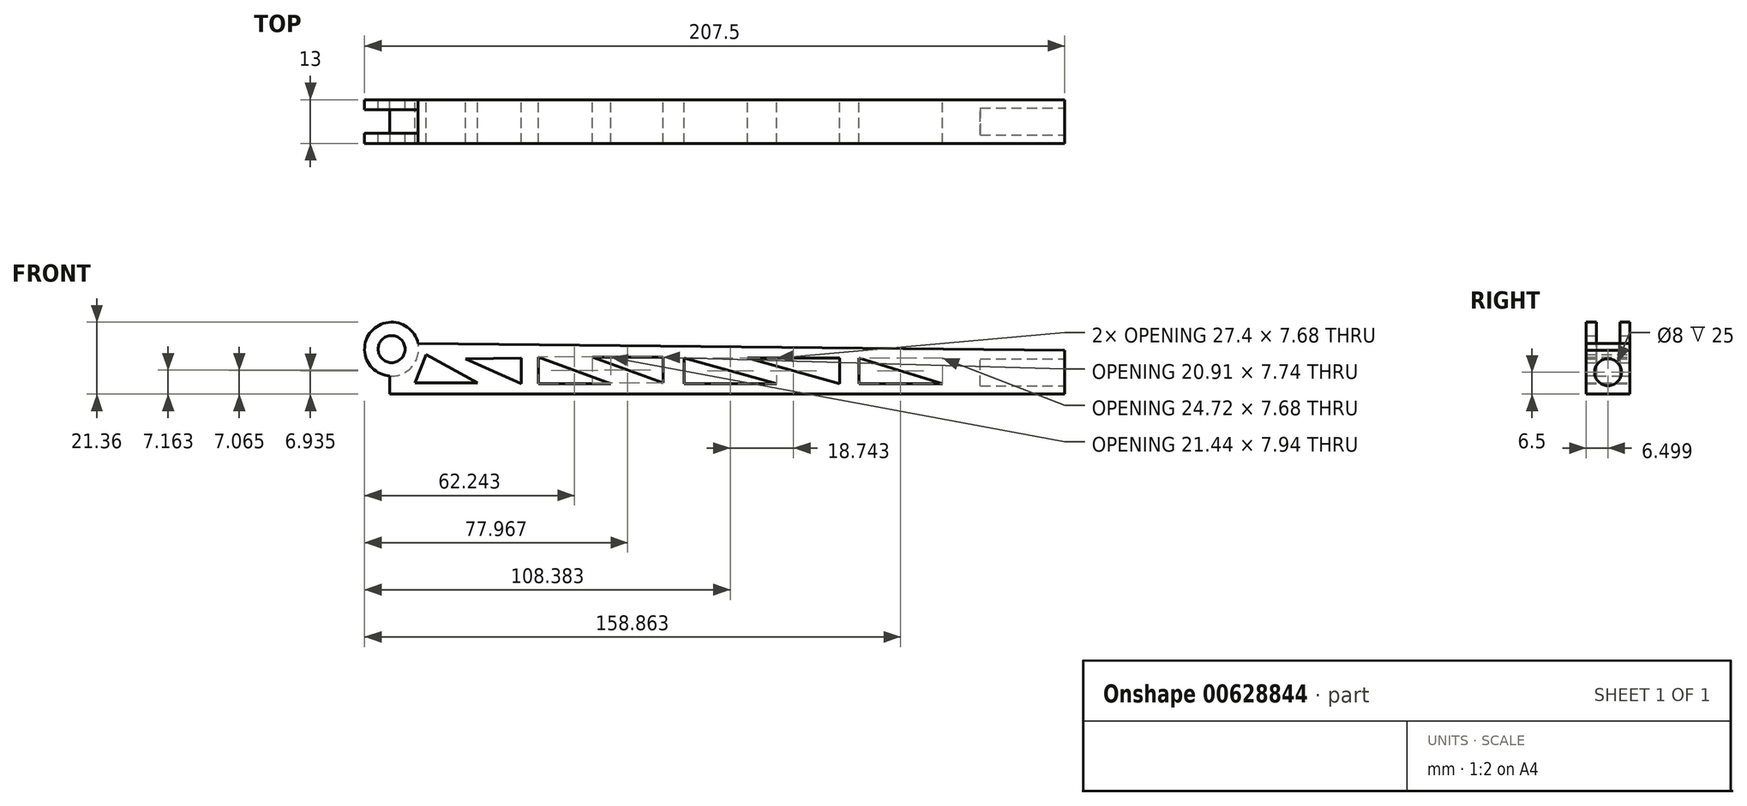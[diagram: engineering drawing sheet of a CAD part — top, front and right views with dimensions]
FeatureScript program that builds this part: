
annotation { "Feature Type Name" : "Feature", "Feature Type Description" : "" }
export const myFeature = defineFeature(function(context is Context, id is Id, definition is map)
    precondition{}
    {
        {
            var Q0;
            Q0=qCreatedBy(makeId("Top.planeOp"),FACE);
            var sketch = newSketch(context, id + "F0", { "sketchPlane" : qUnion([Q0])});
            skLineSegment(sketch, "E0.bottom", {"start": v(-30.92, 10.53) * mm, "end": v(169.08, 10.53) * mm});
            skLineSegment(sketch, "E0.top", {"start": v(-30.92, 23.53) * mm, "end": v(169.08, 23.53) * mm});
            skLineSegment(sketch, "E0.left", {"start": v(-30.92, 10.53) * mm, "end": v(-30.92, 23.53) * mm});
            skLineSegment(sketch, "E0.right", {"start": v(169.08, 10.53) * mm, "end": v(169.08, 23.53) * mm});
            skSolve(sketch);
        }
        {
            var Q0;
            Q0=makeQuery(id+"F0.imprint","IMPRINT",FACE,{"disambiguationData":[TD([[makeQuery(id+"F0.imprint","IMPRINT",EDGE,{"derivedFrom":sQuery(id+"F0.wireOp",EDGE,"E0.bottom")}),1.0]])]});
            extrude(context, id + "F1", {"entities" : qUnion([Q0]), "depth" : 15 * mm, "offsetDistance" : 25 * mm});
        }
        {
            var Q0;
            Q0=makeQuery(id+"F1.opExtrude","SWEPT_FACE",FACE,{"disambiguationData":[OSD([sQuery(id+"F0.wireOp",EDGE,"E0.bottom")])]});
            var sketch = newSketch(context, id + "F2", { "sketchPlane" : qUnion([Q0])});
            skCircle(sketch, "E1", {"center": v(-30.42, 13.36) * mm, "radius": 8 * mm});
            skSolve(sketch);
        }
        {
            var Q0;
            Q0 = qSketchRegion(id + "F2", true);
            extrude(context, id + "F3", {"entities" : qUnion([Q0]), "operationType" : NewBodyOperationType.ADD, "oppositeDirection" : true, "depth" : 3 * mm, "offsetDistance" : 25 * mm});
        }
        {
            var Q0;
            Q0=makeQuery(id+"F1.opExtrude","SWEPT_FACE",FACE,{"disambiguationData":[OSD([sQuery(id+"F0.wireOp",EDGE,"E0.top")])]});
            var sketch = newSketch(context, id + "F4", { "sketchPlane" : qUnion([Q0])});
            skCircle(sketch, "E2", {"center": v(30.42, 13.36) * mm, "radius": 8 * mm});
            skSolve(sketch);
        }
        {
            var Q0;
            Q0 = qSketchRegion(id + "F4", true);
            extrude(context, id + "F5", {"entities" : qUnion([Q0]), "operationType" : NewBodyOperationType.ADD, "oppositeDirection" : true, "depth" : 3 * mm, "offsetDistance" : 25 * mm});
        }
        {
            var Q0;
            Q0=makeQuery(id+"F5.boolean.opBoolean","MERGE",FACE,{"derivedFrom":[makeQuery(id+"F1.opExtrude","SWEPT_FACE",FACE,{"disambiguationData":[OSD([sQuery(id+"F0.wireOp",EDGE,"E0.top")])]}),makeQuery(id+"F5.opExtrude","CAP_FACE",FACE,{"disambiguationData":[OSD([sQuery(id+"F4.wireOp",EDGE,"E2")])],"isStart":true})]});
            var sketch = newSketch(context, id + "F6", { "sketchPlane" : qUnion([Q0])});
            skCircle(sketch, "E3", {"center": v(30.42, 13.36) * mm, "radius": 4 * mm});
            skSolve(sketch);
        }
        {
            var Q0;
            Q0 = qSketchRegion(id + "F6", true);
            extrude(context, id + "F7", {"entities" : qUnion([Q0]), "operationType" : NewBodyOperationType.REMOVE, "oppositeDirection" : true, "depth" : 13 * mm, "offsetDistance" : 25 * mm});
        }
        {
            var Q0;
            Q0=makeQuery(id+"F5.opExtrude","CAP_FACE",FACE,{"disambiguationData":[OSD([sQuery(id+"F4.wireOp",EDGE,"E2")])],"isStart":false});
            var sketch = newSketch(context, id + "F8", { "sketchPlane" : qUnion([Q0])});
            skCircle(sketch, "E4", {"center": v(-30.42, 13.36) * mm, "radius": 8 * mm});
            skSolve(sketch);
        }
        {
            var Q0;
            Q0 = qSketchRegion(id + "F8", true);
            extrude(context, id + "F9", {"entities" : qUnion([Q0]), "operationType" : NewBodyOperationType.REMOVE, "depth" : 7 * mm, "offsetDistance" : 25 * mm});
        }
        {
            var Q0;
            Q0=makeQuery(id+"F3.boolean.opBoolean","MERGE",FACE,{"derivedFrom":[makeQuery(id+"F1.opExtrude","SWEPT_FACE",FACE,{"disambiguationData":[OSD([sQuery(id+"F0.wireOp",EDGE,"E0.bottom")])]}),makeQuery(id+"F3.opExtrude","CAP_FACE",FACE,{"disambiguationData":[OSD([sQuery(id+"F2.wireOp",EDGE,"E1")])],"isStart":true})]});
            var sketch = newSketch(context, id + "F10", { "sketchPlane" : qUnion([Q0])});
            skLineSegment(sketch, "E5", {"start": v(-22.59, 15) * mm, "end": v(169.08, 13) * mm});
            skSolve(sketch);
        }
        {
            var Q0;
            {var subQ0=sQuery(id+"F10.wireOp",EDGE,"E5");Q0=makeQuery(id+"F10.imprint","IMPRINT",FACE,{"disambiguationData":[TD([[makeQuery(id+"F10.imprint","IMPRINT",EDGE,{"derivedFrom":subQ0}),1.0]])]});}
            extrude(context, id + "F11", {"entities" : qUnion([Q0]), "operationType" : NewBodyOperationType.REMOVE, "oppositeDirection" : true, "depth" : 25 * mm, "offsetDistance" : 25 * mm});
        }
        {
            var Q0;
            Q0=makeQuery(id+"F1.opExtrude","SWEPT_FACE",FACE,{"disambiguationData":[OSD([sQuery(id+"F0.wireOp",EDGE,"E0.right")])]});
            var sketch = newSketch(context, id + "F12", { "sketchPlane" : qUnion([Q0])});
            skCircle(sketch, "E6", {"center": v(17.03, 6.5) * mm, "radius": 4 * mm});
            skSolve(sketch);
        }
        {
            var Q0;
            Q0=makeQuery(id+"F12.imprint","IMPRINT",FACE,{"disambiguationData":[TD([[makeQuery(id+"F12.imprint","IMPRINT",EDGE,{"derivedFrom":sQuery(id+"F12.wireOp",EDGE,"E6")}),1.0]])]});
            extrude(context, id + "F13", {"entities" : qUnion([Q0]), "operationType" : NewBodyOperationType.REMOVE, "oppositeDirection" : true, "depth" : 25 * mm, "offsetDistance" : 25 * mm});
        }
        {
            var Q0;
            Q0=makeQuery(id+"F5.boolean.opBoolean","MERGE",FACE,{"derivedFrom":[makeQuery(id+"F1.opExtrude","SWEPT_FACE",FACE,{"disambiguationData":[OSD([sQuery(id+"F0.wireOp",EDGE,"E0.top")])]}),makeQuery(id+"F5.opExtrude","CAP_FACE",FACE,{"disambiguationData":[OSD([sQuery(id+"F4.wireOp",EDGE,"E2")])],"isStart":true})]});
            var sketch = newSketch(context, id + "F14", { "sketchPlane" : qUnion([Q0])});
            skLineSegment(sketch, "E7", {"start": v(20.2, 11.75) * mm, "end": v(23.44, 3.36) * mm});
            skLineSegment(sketch, "E8", {"start": v(23.44, 3.36) * mm, "end": v(5, 3.36) * mm});
            skLineSegment(sketch, "E9", {"start": v(5, 3.36) * mm, "end": v(20.2, 11.75) * mm});
            skLineSegment(sketch, "E10", {"start": v(8.48, 10.46) * mm, "end": v(-8.02, 3.1) * mm});
            skLineSegment(sketch, "E11", {"start": v(-8.02, 3.1) * mm, "end": v(-8.02, 10.75) * mm});
            skLineSegment(sketch, "E12", {"start": v(-8.02, 10.75) * mm, "end": v(8.48, 10.46) * mm});
            skLineSegment(sketch, "E13", {"start": v(-13.1, 3.1) * mm, "end": v(-34.54, 3.1) * mm});
            skLineSegment(sketch, "E14", {"start": v(-34.54, 3.1) * mm, "end": v(-13.1, 11.03) * mm});
            skLineSegment(sketch, "E15", {"start": v(-13.1, 11.03) * mm, "end": v(-13.1, 3.1) * mm});
            skLineSegment(sketch, "E16", {"start": v(-29.1, 11.03) * mm, "end": v(-50, 3.3) * mm});
            skLineSegment(sketch, "E17", {"start": v(-50, 3.3) * mm, "end": v(-50, 11.03) * mm});
            skLineSegment(sketch, "E18", {"start": v(-50, 11.03) * mm, "end": v(-29.1, 11.03) * mm});
            skLineSegment(sketch, "E19", {"start": v(-56.26, 3.1) * mm, "end": v(-83.66, 3.1) * mm});
            skLineSegment(sketch, "E20", {"start": v(-83.66, 3.1) * mm, "end": v(-56.26, 10.77) * mm});
            skLineSegment(sketch, "E21", {"start": v(-56.26, 10.77) * mm, "end": v(-56.26, 3.1) * mm});
            skLineSegment(sketch, "E22", {"start": v(-75, 10.77) * mm, "end": v(-102.4, 3.1) * mm});
            skLineSegment(sketch, "E23", {"start": v(-102.4, 3.1) * mm, "end": v(-102.4, 10.77) * mm});
            skLineSegment(sketch, "E24", {"start": v(-102.4, 10.77) * mm, "end": v(-75, 10.77) * mm});
            skLineSegment(sketch, "E25", {"start": v(-108.08, 3.1) * mm, "end": v(-132.8, 3.1) * mm});
            skLineSegment(sketch, "E26", {"start": v(-132.8, 3.1) * mm, "end": v(-108.08, 10.77) * mm});
            skLineSegment(sketch, "E27", {"start": v(-108.08, 10.77) * mm, "end": v(-108.08, 3.1) * mm});
            skSolve(sketch);
        }
        {
            var Q0;
            Q0=makeQuery(id+"F14.imprint","IMPRINT",FACE,{"disambiguationData":[TD([[makeQuery(id+"F14.imprint","IMPRINT",EDGE,{"derivedFrom":sQuery(id+"F14.wireOp",EDGE,"E7")}),-1.0]])]});
            var Q1;
            Q1=makeQuery(id+"F14.imprint","IMPRINT",FACE,{"disambiguationData":[TD([[makeQuery(id+"F14.imprint","IMPRINT",EDGE,{"derivedFrom":sQuery(id+"F14.wireOp",EDGE,"E10")}),-1.0]])]});
            var Q2;
            Q2=makeQuery(id+"F14.imprint","IMPRINT",FACE,{"disambiguationData":[TD([[makeQuery(id+"F14.imprint","IMPRINT",EDGE,{"derivedFrom":sQuery(id+"F14.wireOp",EDGE,"E13")}),-1.0]])]});
            var Q3;
            Q3=makeQuery(id+"F14.imprint","IMPRINT",FACE,{"disambiguationData":[TD([[makeQuery(id+"F14.imprint","IMPRINT",EDGE,{"derivedFrom":sQuery(id+"F14.wireOp",EDGE,"E16")}),-1.0]])]});
            var Q4;
            Q4=makeQuery(id+"F14.imprint","IMPRINT",FACE,{"disambiguationData":[TD([[makeQuery(id+"F14.imprint","IMPRINT",EDGE,{"derivedFrom":sQuery(id+"F14.wireOp",EDGE,"E19")}),-1.0]])]});
            var Q5;
            Q5=makeQuery(id+"F14.imprint","IMPRINT",FACE,{"disambiguationData":[TD([[makeQuery(id+"F14.imprint","IMPRINT",EDGE,{"derivedFrom":sQuery(id+"F14.wireOp",EDGE,"E22")}),-1.0]])]});
            var Q6;
            Q6=makeQuery(id+"F14.imprint","IMPRINT",FACE,{"disambiguationData":[TD([[makeQuery(id+"F14.imprint","IMPRINT",EDGE,{"derivedFrom":sQuery(id+"F14.wireOp",EDGE,"E25")}),-1.0]])]});
            extrude(context, id + "F15", {"entities" : qUnion([Q0, Q1, Q2, Q3, Q4, Q5, Q6]), "operationType" : NewBodyOperationType.REMOVE, "oppositeDirection" : true, "depth" : 25 * mm, "offsetDistance" : 25 * mm});
        }
    });
